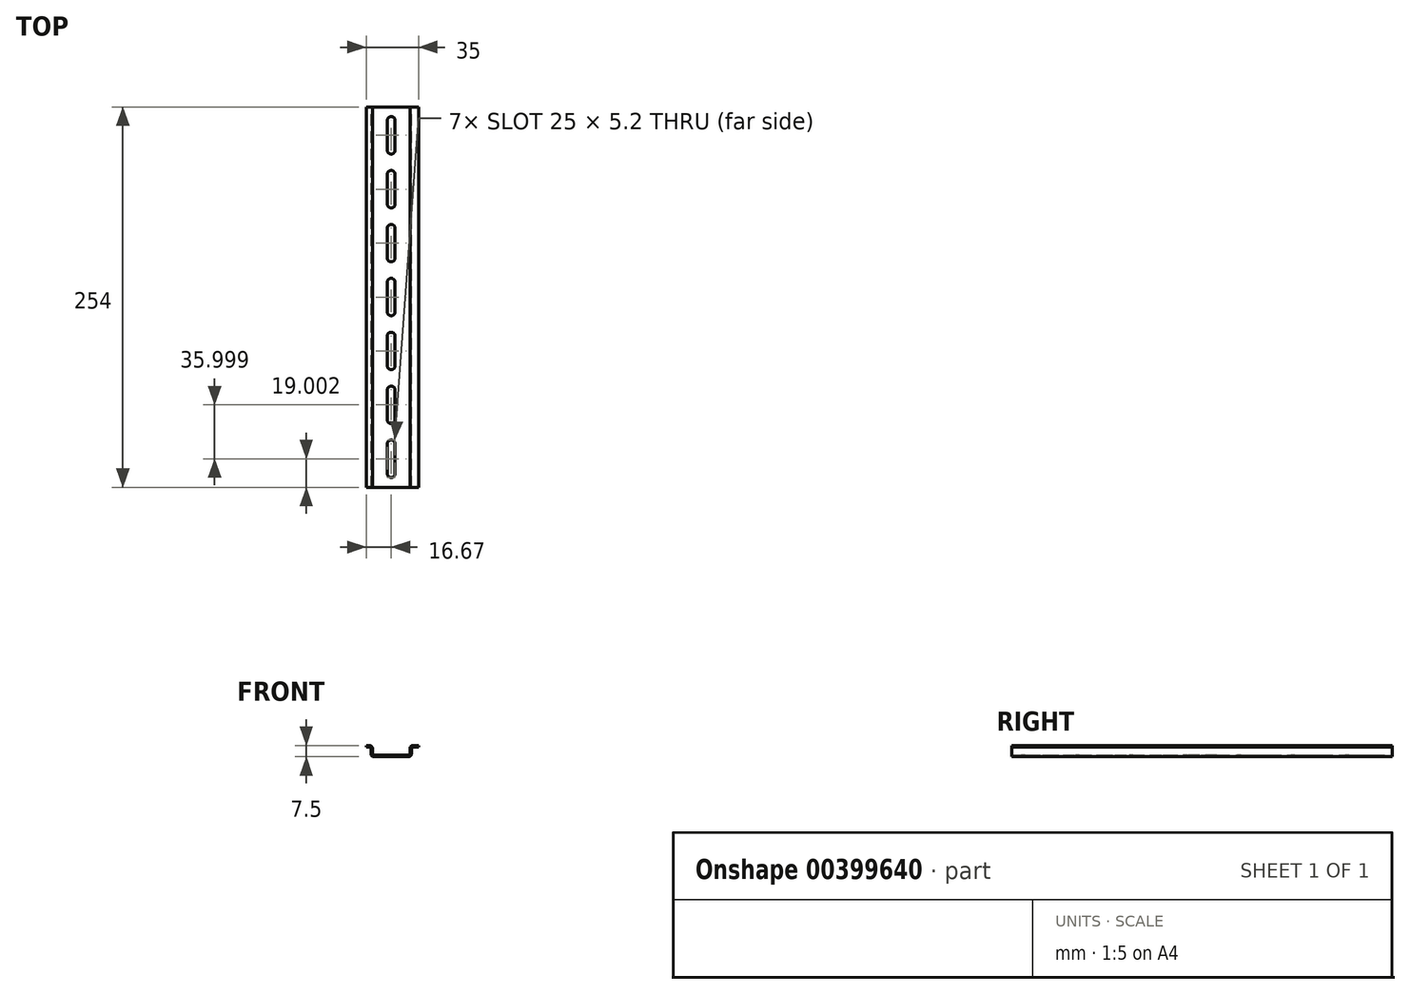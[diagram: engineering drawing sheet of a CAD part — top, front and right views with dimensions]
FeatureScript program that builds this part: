
annotation { "Feature Type Name" : "Feature", "Feature Type Description" : "" }
export const myFeature = defineFeature(function(context is Context, id is Id, definition is map)
    precondition{}
    {
        {
            var Q0;
            Q0=qCreatedBy(makeId("Front.planeOp"),FACE);
            var sketch = newSketch(context, id + "F0", { "sketchPlane" : qUnion([Q0])});
            skLineSegment(sketch, "E0", {"start": v(-11.5, 0) * mm, "end": v(11.5, 0) * mm});
            skLineSegment(sketch, "E1", {"start": v(13.5, 2) * mm, "end": v(13.5, 5.5) * mm});
            skLineSegment(sketch, "E2", {"start": v(14.5, 6.5) * mm, "end": v(18.33, 6.5) * mm});
            skLineSegment(sketch, "E3", {"start": v(18.33, 6.5) * mm, "end": v(18.33, 7.5) * mm});
            skLineSegment(sketch, "E4", {"start": v(18.33, 7.5) * mm, "end": v(14.52, 7.5) * mm});
            skLineSegment(sketch, "E5", {"start": v(12.52, 5.5) * mm, "end": v(12.52, 2) * mm});
            skLineSegment(sketch, "E6", {"start": v(11.52, 1) * mm, "end": v(-11.48, 1) * mm});
            skLineSegment(sketch, "E7", {"start": v(-12.48, 2) * mm, "end": v(-12.48, 5.5) * mm});
            skLineSegment(sketch, "E8", {"start": v(-14.48, 7.5) * mm, "end": v(-16.67, 7.5) * mm});
            skLineSegment(sketch, "E9", {"start": v(-16.67, 7.5) * mm, "end": v(-16.67, 6.5) * mm});
            skLineSegment(sketch, "E10", {"start": v(-16.67, 6.5) * mm, "end": v(-14.5, 6.5) * mm});
            skLineSegment(sketch, "E11", {"start": v(-13.5, 5.5) * mm, "end": v(-13.5, 2) * mm});
            skPoint(sketch, "E12.visualSharp", {"position": v(-12.48, 1) * mm});
            skArc(sketch, "E12.filletArc", {"start": v(-12.48, 2) * mm, "mid": v(-12.2, 1.3) * mm, "end": v(-11.48, 1) * mm});
            skPoint(sketch, "E13.visualSharp", {"position": v(12.52, 1) * mm});
            skArc(sketch, "E13.filletArc", {"start": v(11.52, 1) * mm, "mid": v(12.22, 1.3) * mm, "end": v(12.52, 2) * mm});
            skPoint(sketch, "E14.visualSharp", {"position": v(13.5, 6.5) * mm});
            skArc(sketch, "E14.filletArc", {"start": v(14.5, 6.5) * mm, "mid": v(13.8, 6.2) * mm, "end": v(13.5, 5.5) * mm});
            skPoint(sketch, "E15.visualSharp", {"position": v(-13.5, 6.5) * mm});
            skArc(sketch, "E15.filletArc", {"start": v(-13.5, 5.5) * mm, "mid": v(-13.8, 6.2) * mm, "end": v(-14.5, 6.5) * mm});
            skPoint(sketch, "E16.visualSharp", {"position": v(12.52, 7.5) * mm});
            skArc(sketch, "E16.filletArc", {"start": v(14.52, 7.5) * mm, "mid": v(13.1, 6.92) * mm, "end": v(12.52, 5.5) * mm});
            skPoint(sketch, "E17.visualSharp", {"position": v(13.5, 0) * mm});
            skArc(sketch, "E17.filletArc", {"start": v(11.5, 0) * mm, "mid": v(12.91, 0.59) * mm, "end": v(13.5, 2) * mm});
            skPoint(sketch, "E18.visualSharp", {"position": v(-13.5, 0) * mm});
            skArc(sketch, "E18.filletArc", {"start": v(-13.5, 2) * mm, "mid": v(-12.91, 0.59) * mm, "end": v(-11.5, 0) * mm});
            skPoint(sketch, "E19.visualSharp", {"position": v(-12.48, 7.5) * mm});
            skArc(sketch, "E19.filletArc", {"start": v(-12.48, 5.5) * mm, "mid": v(-13.07, 6.92) * mm, "end": v(-14.48, 7.5) * mm});
            skSolve(sketch);
        }
        {
            var Q0;
            Q0=qSketchRegion(id+"F0",true);
            extrude(context, id + "F1", {"entities" : qUnion([Q0]), "depth" : 254 * mm, "symmetric" : true});
        }
        {
            var Q0;
            Q0=makeQuery(id+"F1.opExtrude","SWEPT_FACE",FACE,{"disambiguationData":[OSD([sQuery(id+"F0.wireOp",EDGE,"E6")])]});
            var sketch = newSketch(context, id + "F2", { "sketchPlane" : qUnion([Q0])});
            skLineSegment(sketch, "E20", {"start": v(-2.6, 9.9) * mm, "end": v(-2.6, -9.9) * mm});
            skArc(sketch, "E21", {"start": v(-2.6, -9.9) * mm, "mid": v(0, -12.5) * mm, "end": v(2.6, -9.9) * mm});
            skLineSegment(sketch, "E22", {"start": v(2.6, -9.9) * mm, "end": v(2.6, 9.9) * mm});
            skArc(sketch, "E23", {"start": v(2.6, 9.9) * mm, "mid": v(0, 12.5) * mm, "end": v(-2.6, 9.9) * mm});
            skLineSegment(sketch, "E24", {"start": v(2.6, 26.1) * mm, "end": v(2.6, 45.9) * mm});
            skLineSegment(sketch, "E25", {"start": v(-2.6, 45.9) * mm, "end": v(-2.6, 26.1) * mm});
            skArc(sketch, "E26", {"start": v(2.6, 45.9) * mm, "mid": v(0, 48.5) * mm, "end": v(-2.6, 45.9) * mm});
            skArc(sketch, "E27", {"start": v(-2.6, 26.1) * mm, "mid": v(0, 23.5) * mm, "end": v(2.6, 26.1) * mm});
            skLineSegment(sketch, "E28", {"start": v(2.6, 62.1) * mm, "end": v(2.6, 81.9) * mm});
            skLineSegment(sketch, "E29", {"start": v(-2.6, 81.9) * mm, "end": v(-2.6, 62.1) * mm});
            skArc(sketch, "E30", {"start": v(2.6, 81.9) * mm, "mid": v(0, 84.5) * mm, "end": v(-2.6, 81.9) * mm});
            skArc(sketch, "E31", {"start": v(-2.6, 62.1) * mm, "mid": v(0, 59.5) * mm, "end": v(2.6, 62.1) * mm});
            skLineSegment(sketch, "E32", {"start": v(2.6, 98.1) * mm, "end": v(2.6, 117.9) * mm});
            skLineSegment(sketch, "E33", {"start": v(-2.6, 117.9) * mm, "end": v(-2.6, 98.1) * mm});
            skArc(sketch, "E34", {"start": v(2.6, 117.9) * mm, "mid": v(0, 120.5) * mm, "end": v(-2.6, 117.9) * mm});
            skArc(sketch, "E35", {"start": v(-2.6, 98.1) * mm, "mid": v(0, 95.5) * mm, "end": v(2.6, 98.1) * mm});
            skLineSegment(sketch, "E36", {"start": v(2.6, -45.9) * mm, "end": v(2.6, -26.1) * mm});
            skLineSegment(sketch, "E37", {"start": v(-2.6, -26.1) * mm, "end": v(-2.6, -45.9) * mm});
            skArc(sketch, "E38", {"start": v(2.6, -26.1) * mm, "mid": v(0, -23.5) * mm, "end": v(-2.6, -26.1) * mm});
            skArc(sketch, "E39", {"start": v(-2.6, -45.9) * mm, "mid": v(0, -48.5) * mm, "end": v(2.6, -45.9) * mm});
            skLineSegment(sketch, "E40", {"start": v(2.6, -81.9) * mm, "end": v(2.6, -62.1) * mm});
            skLineSegment(sketch, "E41", {"start": v(-2.6, -62.1) * mm, "end": v(-2.6, -81.9) * mm});
            skArc(sketch, "E42", {"start": v(2.6, -62.1) * mm, "mid": v(0, -59.5) * mm, "end": v(-2.6, -62.1) * mm});
            skArc(sketch, "E43", {"start": v(-2.6, -81.9) * mm, "mid": v(0, -84.5) * mm, "end": v(2.6, -81.9) * mm});
            skLineSegment(sketch, "E44", {"start": v(2.6, -117.9) * mm, "end": v(2.6, -98.1) * mm});
            skLineSegment(sketch, "E45", {"start": v(-2.6, -98.1) * mm, "end": v(-2.6, -117.9) * mm});
            skArc(sketch, "E46", {"start": v(2.6, -98.1) * mm, "mid": v(0, -95.5) * mm, "end": v(-2.6, -98.1) * mm});
            skArc(sketch, "E47", {"start": v(-2.6, -117.9) * mm, "mid": v(0, -120.5) * mm, "end": v(2.6, -117.9) * mm});
            skSolve(sketch);
        }
        {
            var Q0;
            Q0=qSketchRegion(id+"F2",true);
            extrude(context, id + "F3", {"entities" : qUnion([Q0]), "operationType" : NewBodyOperationType.REMOVE, "endBound" : BoundingType.THROUGH_ALL, "oppositeDirection" : true, "depth" : 25.4 * mm});
        }
    });
